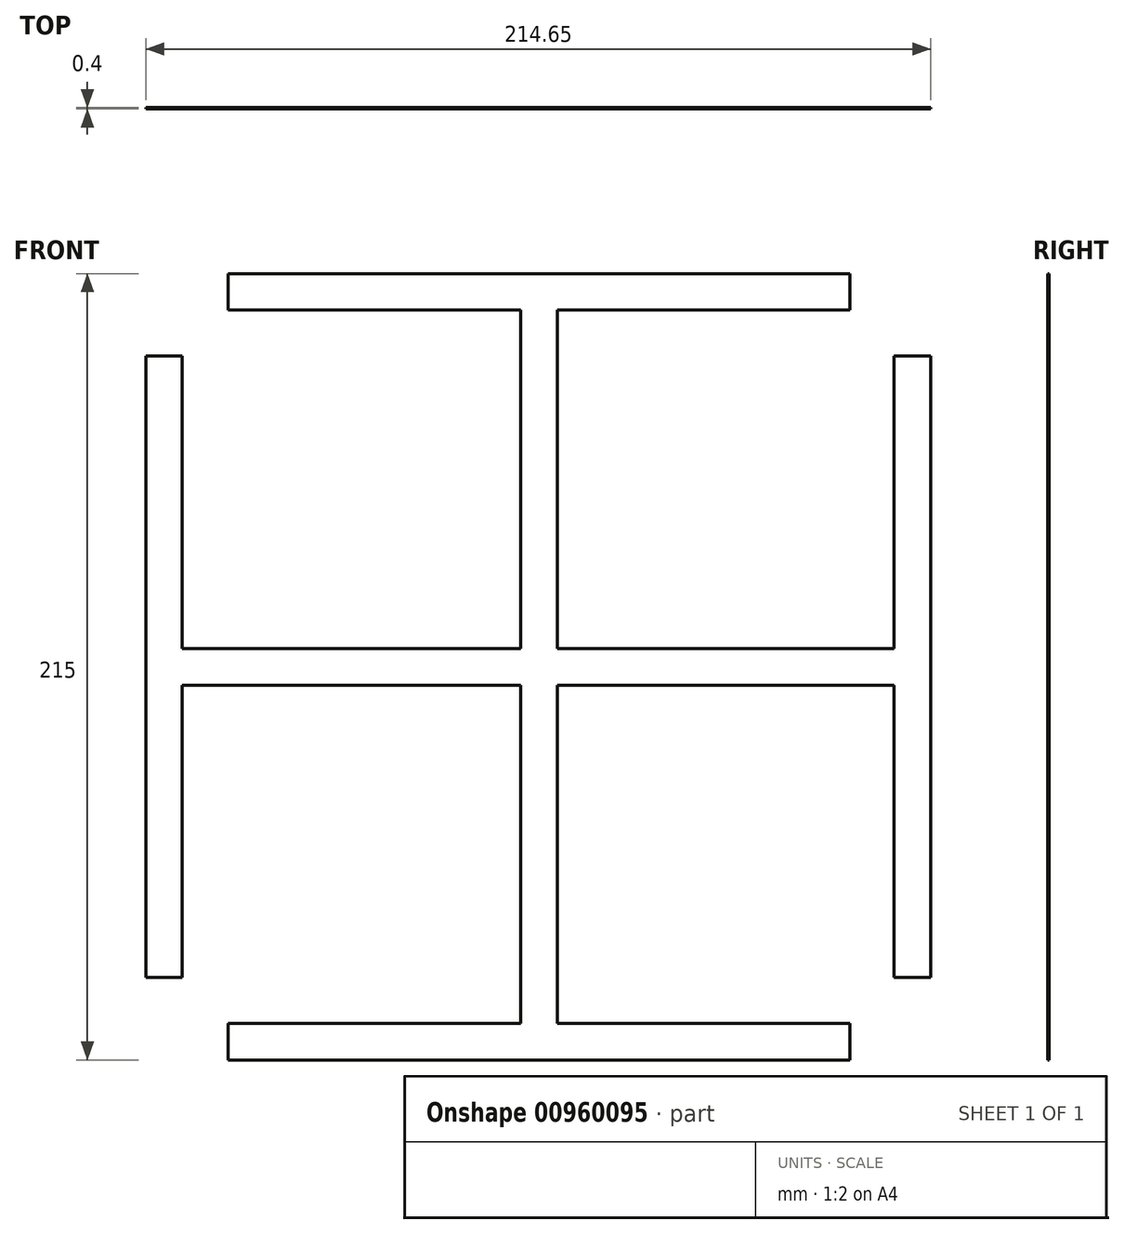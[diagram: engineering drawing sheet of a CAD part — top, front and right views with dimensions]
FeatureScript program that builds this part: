
annotation { "Feature Type Name" : "Feature", "Feature Type Description" : "" }
export const myFeature = defineFeature(function(context is Context, id is Id, definition is map)
    precondition{}
    {
        {
            var Q0;
            Q0=qCreatedBy(makeId("Front.planeOp"),FACE);
            var sketch = newSketch(context, id + "F0", { "sketchPlane" : qUnion([Q0])});
            skLineSegment(sketch, "E0.bottom", {"start": v(-107.5, 5) * mm, "end": v(107.5, 5) * mm});
            skLineSegment(sketch, "E0.top", {"start": v(-107.5, -5) * mm, "end": v(107.5, -5) * mm});
            skLineSegment(sketch, "E0.left", {"start": v(-107.5, 5) * mm, "end": v(-107.5, -5) * mm});
            skLineSegment(sketch, "E0.right", {"start": v(107.5, 5) * mm, "end": v(107.5, -5) * mm});
            skPoint(sketch, "E0.middle", {"position": v(0, 0) * mm});
            skLineSegment(sketch, "E1.bottom", {"start": v(5, 107.5) * mm, "end": v(-5, 107.5) * mm});
            skLineSegment(sketch, "E1.top", {"start": v(5, -107.5) * mm, "end": v(-5, -107.5) * mm});
            skLineSegment(sketch, "E1.left", {"start": v(5, 107.5) * mm, "end": v(5, -107.5) * mm});
            skLineSegment(sketch, "E1.right", {"start": v(-5, 107.5) * mm, "end": v(-5, -107.5) * mm});
            skLineSegment(sketch, "E2.bottom", {"start": v(-5, 107.5) * mm, "end": v(-85, 107.5) * mm});
            skLineSegment(sketch, "E2.top", {"start": v(-5, 97.5) * mm, "end": v(-85, 97.5) * mm});
            skLineSegment(sketch, "E2.left", {"start": v(-5, 107.5) * mm, "end": v(-5, 97.5) * mm});
            skLineSegment(sketch, "E2.right", {"start": v(-85, 107.5) * mm, "end": v(-85, 97.5) * mm});
            skLineSegment(sketch, "E3.bottom", {"start": v(5, 107.5) * mm, "end": v(85, 107.5) * mm});
            skLineSegment(sketch, "E3.top", {"start": v(5, 97.5) * mm, "end": v(85, 97.5) * mm});
            skLineSegment(sketch, "E3.left", {"start": v(5, 107.5) * mm, "end": v(5, 97.5) * mm});
            skLineSegment(sketch, "E3.right", {"start": v(85, 107.5) * mm, "end": v(85, 97.5) * mm});
            skLineSegment(sketch, "E4.bottom", {"start": v(107.15, -5) * mm, "end": v(107.15, 5) * mm});
            skLineSegment(sketch, "E5.bottom", {"start": v(107.15, 5) * mm, "end": v(107.15, 85) * mm});
            skLineSegment(sketch, "E5.top", {"start": v(97.15, 5) * mm, "end": v(97.15, 85) * mm});
            skLineSegment(sketch, "E5.left", {"start": v(107.15, 5) * mm, "end": v(97.15, 5) * mm});
            skLineSegment(sketch, "E5.right", {"start": v(107.15, 85) * mm, "end": v(97.15, 85) * mm});
            skLineSegment(sketch, "E6.bottom", {"start": v(107.15, -5) * mm, "end": v(107.15, -85) * mm});
            skLineSegment(sketch, "E6.top", {"start": v(97.15, -5) * mm, "end": v(97.15, -85) * mm});
            skLineSegment(sketch, "E6.left", {"start": v(107.15, -5) * mm, "end": v(97.15, -5) * mm});
            skLineSegment(sketch, "E6.right", {"start": v(107.15, -85) * mm, "end": v(97.15, -85) * mm});
            skLineSegment(sketch, "E7.bottom", {"start": v(-5, -107.5) * mm, "end": v(5, -107.5) * mm});
            skLineSegment(sketch, "E8.bottom", {"start": v(5, -107.5) * mm, "end": v(85, -107.5) * mm});
            skLineSegment(sketch, "E8.top", {"start": v(5, -97.5) * mm, "end": v(85, -97.5) * mm});
            skLineSegment(sketch, "E8.left", {"start": v(5, -107.5) * mm, "end": v(5, -97.5) * mm});
            skLineSegment(sketch, "E8.right", {"start": v(85, -107.5) * mm, "end": v(85, -97.5) * mm});
            skLineSegment(sketch, "E9.bottom", {"start": v(-5, -107.5) * mm, "end": v(-85, -107.5) * mm});
            skLineSegment(sketch, "E9.top", {"start": v(-5, -97.5) * mm, "end": v(-85, -97.5) * mm});
            skLineSegment(sketch, "E9.left", {"start": v(-5, -107.5) * mm, "end": v(-5, -97.5) * mm});
            skLineSegment(sketch, "E9.right", {"start": v(-85, -107.5) * mm, "end": v(-85, -97.5) * mm});
            skLineSegment(sketch, "E10.bottom", {"start": v(-107.5, -5) * mm, "end": v(-107.5, -85) * mm});
            skLineSegment(sketch, "E10.top", {"start": v(-97.5, -5) * mm, "end": v(-97.5, -85) * mm});
            skLineSegment(sketch, "E10.left", {"start": v(-107.5, -5) * mm, "end": v(-97.5, -5) * mm});
            skLineSegment(sketch, "E10.right", {"start": v(-107.5, -85) * mm, "end": v(-97.5, -85) * mm});
            skLineSegment(sketch, "E11.bottom", {"start": v(-107.5, 5) * mm, "end": v(-107.5, 85) * mm});
            skLineSegment(sketch, "E11.top", {"start": v(-97.5, 5) * mm, "end": v(-97.5, 85) * mm});
            skLineSegment(sketch, "E11.left", {"start": v(-107.5, 5) * mm, "end": v(-97.5, 5) * mm});
            skLineSegment(sketch, "E11.right", {"start": v(-107.5, 85) * mm, "end": v(-97.5, 85) * mm});
            skSolve(sketch);
        }
        {
            var Q0;
            {var subQ0=sQuery(id+"F0.wireOp",EDGE,"E9.bottom");Q0=makeQuery(id+"F0.imprint","IMPRINT",FACE,{"disambiguationData":[TD([[makeQuery(id+"F0.imprint","IMPRINT",EDGE,{"derivedFrom":subQ0}),-1.0]])]});}
            var Q1;
            {var subQ4=sQuery(id+"F0.wireOp",EDGE,"E1.top");Q1=makeQuery(id+"F0.imprint","IMPRINT",FACE,{"disambiguationData":[TD([[makeQuery(id+"F0.imprint","IMPRINT",EDGE,{"derivedFrom":subQ4}),-1.0]])]});}
            var Q2;
            {var subQ0=sQuery(id+"F0.wireOp",EDGE,"E8.bottom");Q2=makeQuery(id+"F0.imprint","IMPRINT",FACE,{"disambiguationData":[TD([[makeQuery(id+"F0.imprint","IMPRINT",EDGE,{"derivedFrom":subQ0}),1.0]])]});}
            var Q3;
            {var subQ0=sQuery(id+"F0.wireOp",EDGE,"E6.bottom");Q3=makeQuery(id+"F0.imprint","IMPRINT",FACE,{"disambiguationData":[TD([[makeQuery(id+"F0.imprint","IMPRINT",EDGE,{"derivedFrom":subQ0}),-1.0]])]});}
            var Q4;
            {var subQ0=sQuery(id+"F0.wireOp",EDGE,"E4.bottom");Q4=makeQuery(id+"F0.imprint","IMPRINT",FACE,{"disambiguationData":[TD([[makeQuery(id+"F0.imprint","IMPRINT",EDGE,{"derivedFrom":subQ0}),1.0]])]});}
            var Q5;
            {var subQ0=sQuery(id+"F0.wireOp",EDGE,"E5.bottom");Q5=makeQuery(id+"F0.imprint","IMPRINT",FACE,{"disambiguationData":[TD([[makeQuery(id+"F0.imprint","IMPRINT",EDGE,{"derivedFrom":subQ0}),1.0]])]});}
            var Q6;
            {var subQ1=sQuery(id+"F0.wireOp",EDGE,"E1.bottom");Q6=makeQuery(id+"F0.imprint","IMPRINT",FACE,{"disambiguationData":[TD([[makeQuery(id+"F0.imprint","IMPRINT",EDGE,{"derivedFrom":subQ1}),1.0]])]});}
            var Q7;
            {var subQ0=sQuery(id+"F0.wireOp",EDGE,"E1.right");var subQ1=sQuery(id+"F0.wireOp",EDGE,"E0.bottom");var subQ2=makeQuery(id+"F0.imprint","INTERSECT",VERTEX,{"derivedFrom":[subQ1,subQ0]});Q7=makeQuery(id+"F0.imprint","IMPRINT",FACE,{"disambiguationData":[TD([[makeQuery(id+"F0.imprint","IMPRINT",EDGE,{"disambiguationData":[TD([[subQ2,-1.0]])],"derivedFrom":subQ1}),-1.0]])]});}
            var Q8;
            {var subQ6=sQuery(id+"F0.wireOp",EDGE,"E0.left");Q8=makeQuery(id+"F0.imprint","IMPRINT",FACE,{"disambiguationData":[TD([[makeQuery(id+"F0.imprint","IMPRINT",EDGE,{"derivedFrom":subQ6}),1.0]])]});}
            var Q9;
            {var subQ2=sQuery(id+"F0.wireOp",EDGE,"E10.bottom");Q9=makeQuery(id+"F0.imprint","IMPRINT",FACE,{"disambiguationData":[TD([[makeQuery(id+"F0.imprint","IMPRINT",EDGE,{"derivedFrom":subQ2}),1.0]])]});}
            var Q10;
            {var subQ2=sQuery(id+"F0.wireOp",EDGE,"E11.bottom");Q10=makeQuery(id+"F0.imprint","IMPRINT",FACE,{"disambiguationData":[TD([[makeQuery(id+"F0.imprint","IMPRINT",EDGE,{"derivedFrom":subQ2}),-1.0]])]});}
            var Q11;
            {var subQ0=sQuery(id+"F0.wireOp",EDGE,"E3.bottom");Q11=makeQuery(id+"F0.imprint","IMPRINT",FACE,{"disambiguationData":[TD([[makeQuery(id+"F0.imprint","IMPRINT",EDGE,{"derivedFrom":subQ0}),-1.0]])]});}
            var Q12;
            {var subQ0=sQuery(id+"F0.wireOp",EDGE,"E2.bottom");Q12=makeQuery(id+"F0.imprint","IMPRINT",FACE,{"disambiguationData":[TD([[makeQuery(id+"F0.imprint","IMPRINT",EDGE,{"derivedFrom":subQ0}),1.0]])]});}
            extrude(context, id + "F1", {"entities" : qUnion([Q0, Q1, Q2, Q3, Q4, Q5, Q6, Q7, Q8, Q9, Q10, Q11, Q12]), "depth" : 0.4 * mm, "offsetDistance" : 25 * mm});
        }
    });
